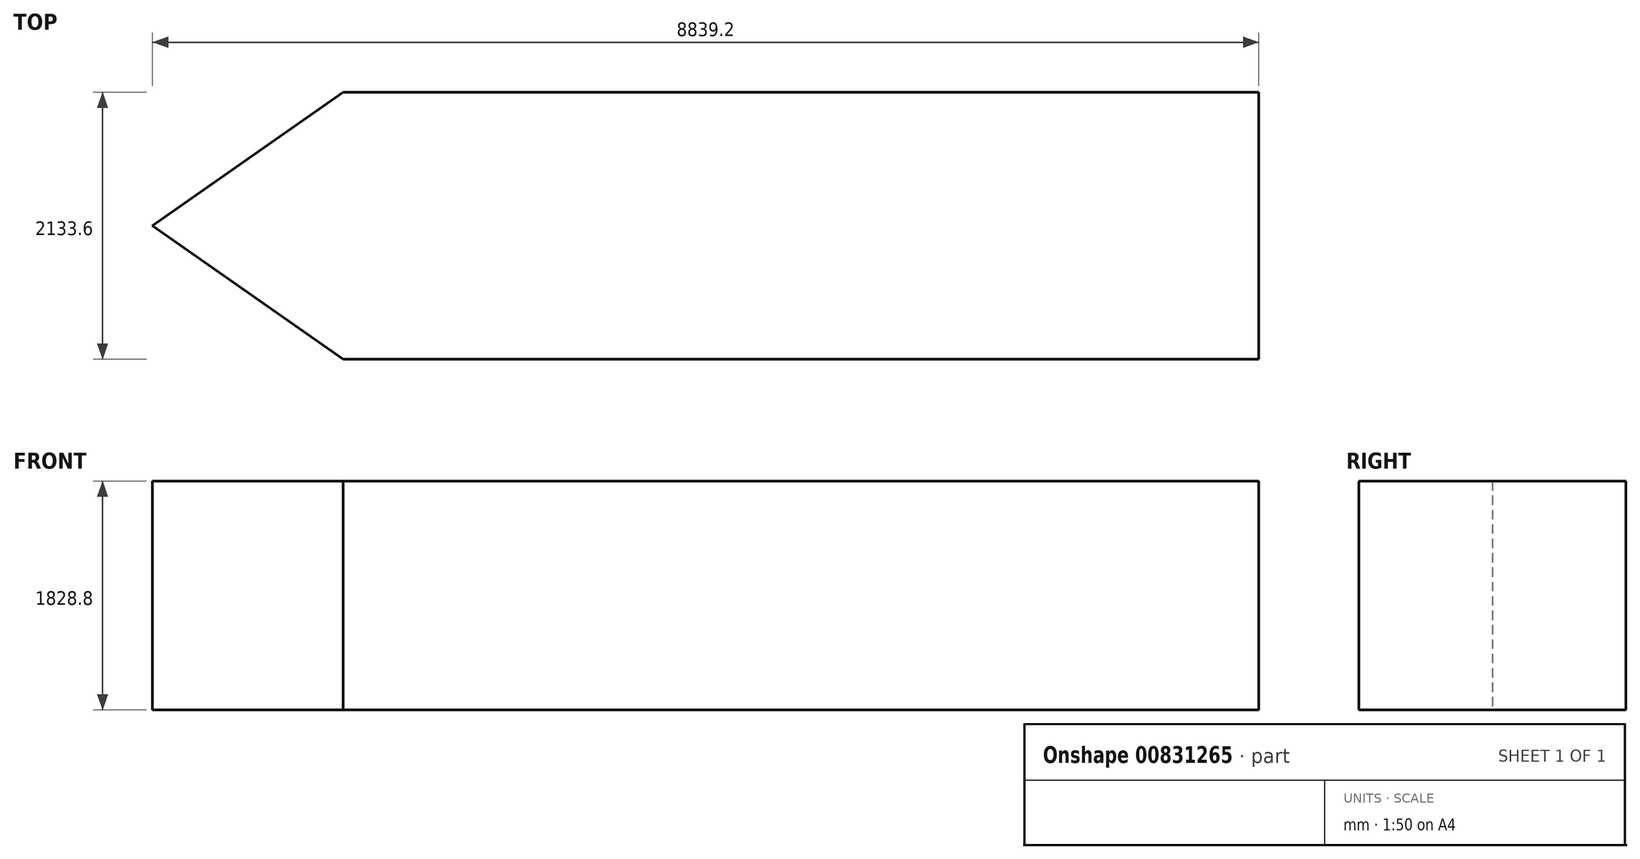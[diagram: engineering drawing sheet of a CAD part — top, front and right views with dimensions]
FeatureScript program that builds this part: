
annotation { "Feature Type Name" : "Feature", "Feature Type Description" : "" }
export const myFeature = defineFeature(function(context is Context, id is Id, definition is map)
    precondition{}
    {
        {
            var Q0;
            Q0=qCreatedBy(makeId("Top.planeOp"),FACE);
            var sketch = newSketch(context, id + "F0", { "sketchPlane" : qUnion([Q0])});
            skLineSegment(sketch, "E0.bottom", {"start": v(4419.6, 1066.8) * mm, "end": v(-2895.6, 1066.8) * mm});
            skLineSegment(sketch, "E0.top", {"start": v(4419.6, -1066.8) * mm, "end": v(-2895.6, -1066.8) * mm});
            skLineSegment(sketch, "E0.left", {"start": v(4419.6, 1066.8) * mm, "end": v(4419.6, -1066.8) * mm});
            skLineSegment(sketch, "E0.right", {"start": v(-4419.6, 1066.8) * mm, "end": v(-4419.6, -1066.8) * mm, "construction": true});
            skPoint(sketch, "E0.middle", {"position": v(0, 0) * mm});
            skLineSegment(sketch, "E1", {"start": v(-2895.6, 1066.8) * mm, "end": v(-4419.6, 0) * mm});
            skLineSegment(sketch, "E2", {"start": v(-4419.6, 0) * mm, "end": v(-2895.6, -1066.8) * mm});
            skLineSegment(sketch, "E3", {"start": v(-2895.6, -1066.8) * mm, "end": v(-2895.6, 1066.8) * mm, "construction": true});
            skLineSegment(sketch, "E4", {"start": v(-2895.6, -1066.8) * mm, "end": v(-4419.6, -1066.8) * mm, "construction": true});
            skLineSegment(sketch, "E5", {"start": v(-4419.6, 1066.8) * mm, "end": v(-2895.6, 1066.8) * mm, "construction": true});
            skSolve(sketch);
        }
        {
            var Q0;
            Q0 = qSketchRegion(id + "F0", true);
            extrude(context, id + "F1", {"entities" : qUnion([Q0]), "depth" : 1828.8 * mm, "offsetDistance" : 25.4 * mm});
        }
    });
